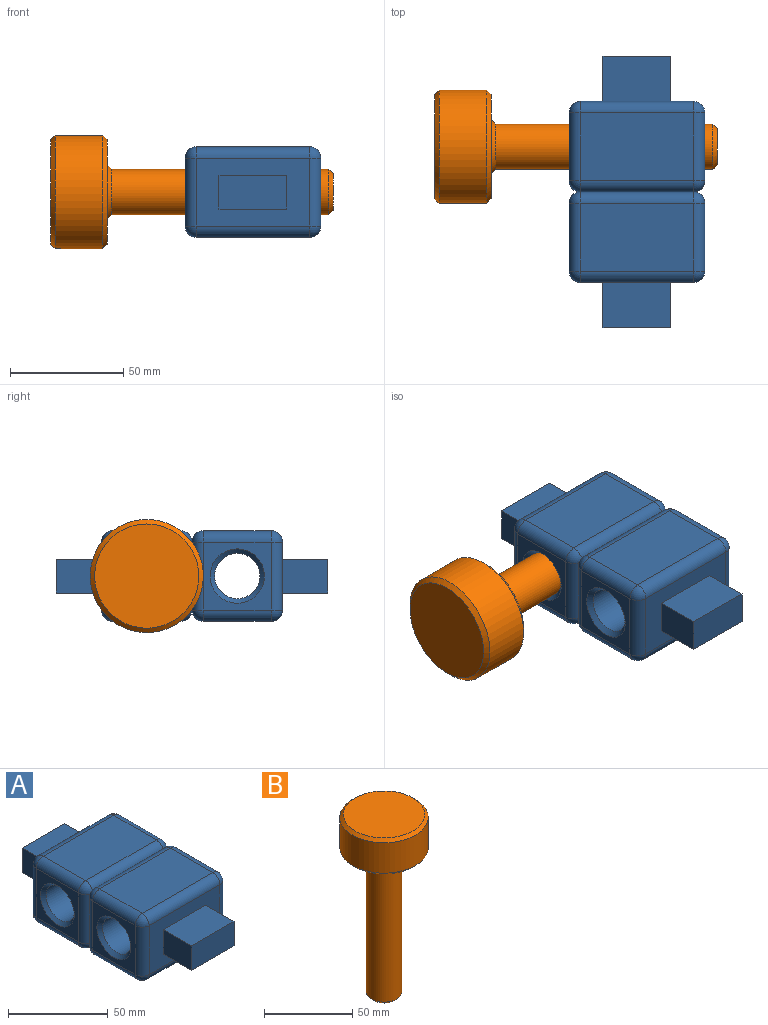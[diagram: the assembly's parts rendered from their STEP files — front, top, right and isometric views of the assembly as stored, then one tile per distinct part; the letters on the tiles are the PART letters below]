
ASSEMBLY  parts=2 mates=2
PART A: 66 faces, bbox 60x120x40 mm
  f0: plane 30x30mm, normal (-1,0,0), area 447.6mm2, adj f13,f18,f21,f24,f27
  f1: plane 30x30mm, normal (1,0,0), area 447.6mm2, adj f5,f9,f10,f11,f26
  f2: plane 50x30mm, normal (0,1,0), area 1050mm2, adj f5,f8,f12,f13,f28,f29,f30,f31
  f3: plane 50x30mm, normal (0,0,1), area 1500mm2, adj f8,f9,f18,f19
  f4: plane 50x30mm, normal (0,0,-1), area 1500mm2, adj f11,f12,f20,f21
  f5: cylinder r=5mm len=30mm, axis (0,0,1), area 235.6mm2, adj f1,f2,f6,f7
  f6: sphere r=5mm, area 39.3mm2, adj f5,f8,f9
  f7: sphere r=5mm, area 39.3mm2, adj f5,f11,f12
  f8: cylinder r=5mm len=50mm, axis (1,0,0), area 392.7mm2, adj f2,f3,f6,f14
  f9: cylinder r=5mm len=30mm, axis (0,-1,0), area 235.6mm2, adj f1,f3,f6,f15
  f10: cylinder r=5mm len=30mm, axis (0,0,-1), area 235.6mm2, adj f1,f15,f16,f43
  f11: cylinder r=5mm len=30mm, axis (0,1,0), area 235.6mm2, adj f1,f4,f7,f16
  f12: cylinder r=5mm len=50mm, axis (-1,0,0), area 392.7mm2, adj f2,f4,f7,f17
  f13: cylinder r=5mm len=30mm, axis (0,0,-1), area 235.6mm2, adj f0,f2,f14,f17
  f14: sphere r=5mm, area 39.3mm2, adj f8,f13,f18
  f15: sphere r=5mm, area 39.3mm2, adj f9,f10,f19
  f16: sphere r=5mm, area 39.3mm2, adj f10,f11,f20
  f17: sphere r=5mm, area 39.3mm2, adj f12,f13,f21
  f18: cylinder r=5mm len=30mm, axis (0,1,0), area 235.6mm2, adj f0,f3,f14,f22
  f19: cylinder r=5mm len=50mm, axis (-1,0,0), area 392.7mm2, adj f3,f15,f22,f52
  f20: cylinder r=5mm len=50mm, axis (1,0,0), area 392.7mm2, adj f4,f16,f23,f53
  f21: cylinder r=5mm len=30mm, axis (0,-1,0), area 235.6mm2, adj f0,f4,f17,f23
  f22: sphere r=5mm, area 39.3mm2, adj f18,f19,f24
  f23: sphere r=5mm, area 39.3mm2, adj f20,f21,f24
  f24: cylinder r=5mm len=30mm, axis (0,0,1), area 235.6mm2, adj f0,f22,f23,f57
  f25: cylinder r=10mm len=56mm, axis (1,0,0), area 3518.6mm2, adj f26,f27
  f26: cone r=10mm half-angle=45deg, axis (1,0,0), area 195.5mm2, adj f1,f25
  f27: cone r=12mm half-angle=45deg, axis (-1,0,0), area 195.5mm2, adj f0,f25
  f28: plane 30x20mm, normal (0,0,1), area 600mm2, adj f2,f29,f31,f32
  f29: plane 20x15mm, normal (1,0,0), area 300mm2, adj f2,f28,f30,f32
  f30: plane 30x20mm, normal (0,0,-1), area 600mm2, adj f2,f29,f31,f32
  f31: plane 20x15mm, normal (-1,0,0), area 300mm2, adj f2,f28,f30,f32
  f32: plane 30x15mm, normal (0,1,0), area 450mm2, adj f28,f29,f30,f31
  f33: plane 30x30mm, normal (-1,0,0), area 447.6mm2, adj f46,f51,f54,f57,f60
  f34: plane 30x30mm, normal (1,0,0), area 447.6mm2, adj f38,f42,f43,f44,f59
  f35: plane 50x30mm, normal (0,-1,0), area 1050mm2, adj f38,f41,f45,f46,f61,f62,f63,f64
  f36: plane 50x30mm, normal (0,0,1), area 1500mm2, adj f41,f42,f51,f52
  f37: plane 50x30mm, normal (0,0,-1), area 1500mm2, adj f44,f45,f53,f54
  f38: cylinder r=5mm len=30mm, axis (0,0,1), area 235.6mm2, adj f34,f35,f39,f40
  f39: sphere r=5mm, area 39.3mm2, adj f38,f41,f42
  f40: sphere r=5mm, area 39.3mm2, adj f38,f44,f45
  f41: cylinder r=5mm len=50mm, axis (1,0,0), area 392.7mm2, adj f35,f36,f39,f47
  f42: cylinder r=5mm len=30mm, axis (0,1,0), area 235.6mm2, adj f34,f36,f39,f48
  f43: cylinder r=5mm len=30mm, axis (0,0,-1), area 235.6mm2, adj f10,f34,f48,f49
  f44: cylinder r=5mm len=30mm, axis (0,-1,0), area 235.6mm2, adj f34,f37,f40,f49
  f45: cylinder r=5mm len=50mm, axis (-1,0,0), area 392.7mm2, adj f35,f37,f40,f50
  f46: cylinder r=5mm len=30mm, axis (0,0,-1), area 235.6mm2, adj f33,f35,f47,f50
  f47: sphere r=5mm, area 39.3mm2, adj f41,f46,f51
  f48: sphere r=5mm, area 39.3mm2, adj f42,f43,f52
  f49: sphere r=5mm, area 39.3mm2, adj f43,f44,f53
  f50: sphere r=5mm, area 39.3mm2, adj f45,f46,f54
  f51: cylinder r=5mm len=30mm, axis (0,-1,0), area 235.6mm2, adj f33,f36,f47,f55
  f52: cylinder r=5mm len=50mm, axis (-1,0,0), area 392.7mm2, adj f19,f36,f48,f55
  f53: cylinder r=5mm len=50mm, axis (1,0,0), area 392.7mm2, adj f20,f37,f49,f56
  f54: cylinder r=5mm len=30mm, axis (0,1,0), area 235.6mm2, adj f33,f37,f50,f56
  f55: sphere r=5mm, area 39.3mm2, adj f51,f52,f57
  f56: sphere r=5mm, area 39.3mm2, adj f53,f54,f57
  f57: cylinder r=5mm len=30mm, axis (0,0,1), area 235.6mm2, adj f24,f33,f55,f56
  f58: cylinder r=10mm len=56mm, axis (1,0,0), area 3518.6mm2, adj f59,f60
  f59: cone r=10mm half-angle=45deg, axis (1,0,0), area 195.5mm2, adj f34,f58
  f60: cone r=12mm half-angle=45deg, axis (-1,0,0), area 195.5mm2, adj f33,f58
  f61: plane 30x20mm, normal (0,0,1), area 600mm2, adj f35,f62,f64,f65
  f62: plane 20x15mm, normal (1,0,0), area 300mm2, adj f35,f61,f63,f65
  f63: plane 30x20mm, normal (0,0,-1), area 600mm2, adj f35,f62,f64,f65
  f64: plane 20x15mm, normal (-1,0,0), area 300mm2, adj f35,f61,f63,f65
  f65: plane 30x15mm, normal (0,-1,0), area 450mm2, adj f61,f62,f63,f64
PART B: 9 faces, bbox 50x50x125 mm
  f0: cylinder r=10mm len=96mm, axis (0,0,-1), area 6031.9mm2, adj f5,f8
  f1: plane 16x16mm, normal (0,0,-1), area 201.1mm2, adj f8
  f2: cylinder r=25mm len=50mm, axis (0,0,-1), area 3298.7mm2, adj f6,f7
  f3: plane 46x46mm, normal (0,0,1), area 1661.9mm2, adj f6
  f4: plane 46x46mm, normal (0,0,-1), area 1209.5mm2, adj f5,f7
  f5: cone r=12mm half-angle=45deg, axis (0,0,1), area 195.5mm2, adj f0,f4
  f6: cone r=23mm half-angle=45deg, axis (0,0,-1), area 426.5mm2, adj f2,f3
  f7: cone r=25mm half-angle=45deg, axis (0,0,1), area 426.5mm2, adj f2,f4
  f8: cone r=10mm half-angle=45deg, axis (0,0,1), area 159.9mm2, adj f0,f1
PLACE A t=(-10.1,36.42,59.03)mm
PLACE B rot(axis=(0,-1,0),90deg) t=(55.47,56.42,79.03)mm
MATE parallel B.f2 <-> A.f25  axis (1,0,0) through (-44.53,56.42,79.03)mm
MATE slider B.f0 <-> A.f25  axis (1,0,0) through (5.47,56.42,79.03)mm
